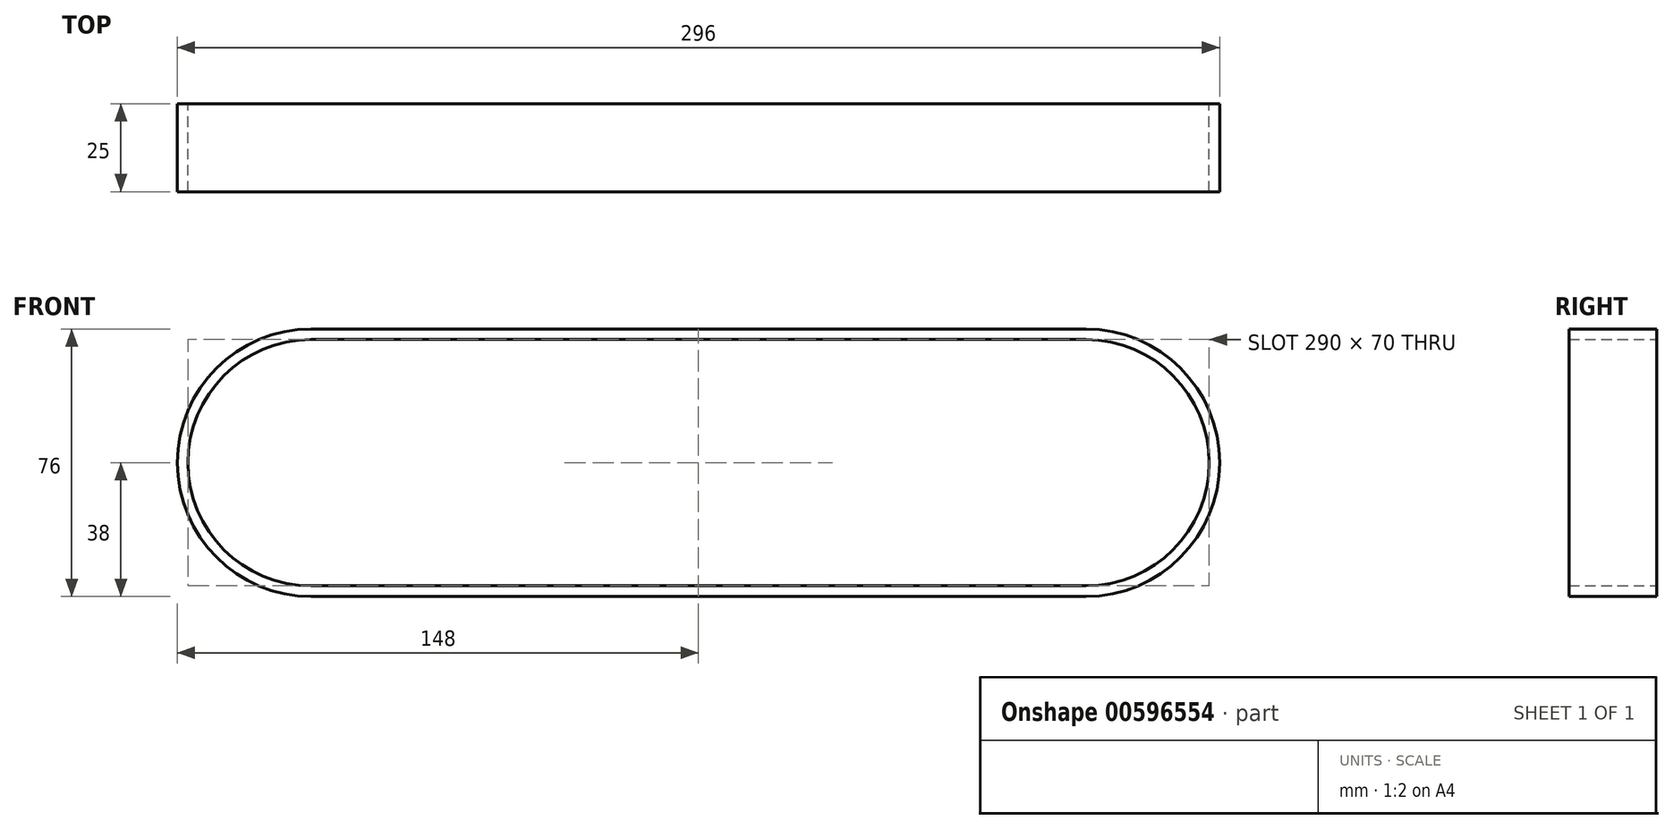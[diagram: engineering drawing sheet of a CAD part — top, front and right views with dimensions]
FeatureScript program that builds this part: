
annotation { "Feature Type Name" : "Feature", "Feature Type Description" : "" }
export const myFeature = defineFeature(function(context is Context, id is Id, definition is map)
    precondition{}
    {
        {
            var Q0;
            Q0=qCreatedBy(makeId("Front.planeOp"),FACE);
            var sketch = newSketch(context, id + "F0", { "sketchPlane" : qUnion([Q0])});
            skArc(sketch, "E0", {"start": v(220, -35) * mm, "mid": v(255, 0) * mm, "end": v(220, 35) * mm});
            skArc(sketch, "E1", {"start": v(0, 35) * mm, "mid": v(-35, 0) * mm, "end": v(0, -35) * mm});
            skArc(sketch, "E2", {"start": v(0, 38) * mm, "mid": v(-38, 0) * mm, "end": v(0, -38) * mm});
            skArc(sketch, "E3", {"start": v(220, -38) * mm, "mid": v(258, 0) * mm, "end": v(220, 38) * mm});
            skLineSegment(sketch, "E4", {"start": v(0, 38) * mm, "end": v(220, 38) * mm});
            skLineSegment(sketch, "E5", {"start": v(0, 35) * mm, "end": v(220, 35) * mm});
            skLineSegment(sketch, "E6", {"start": v(220, -35) * mm, "end": v(0, -35) * mm});
            skLineSegment(sketch, "E7", {"start": v(0, -38) * mm, "end": v(220, -38) * mm});
            skSolve(sketch);
        }
        {
            var Q0;
            Q0 = qSketchRegion(id + "F0", true);
            extrude(context, id + "F1", {"entities" : qUnion([Q0]), "depth" : 25 * mm, "offsetDistance" : 25 * mm});
        }
    });
